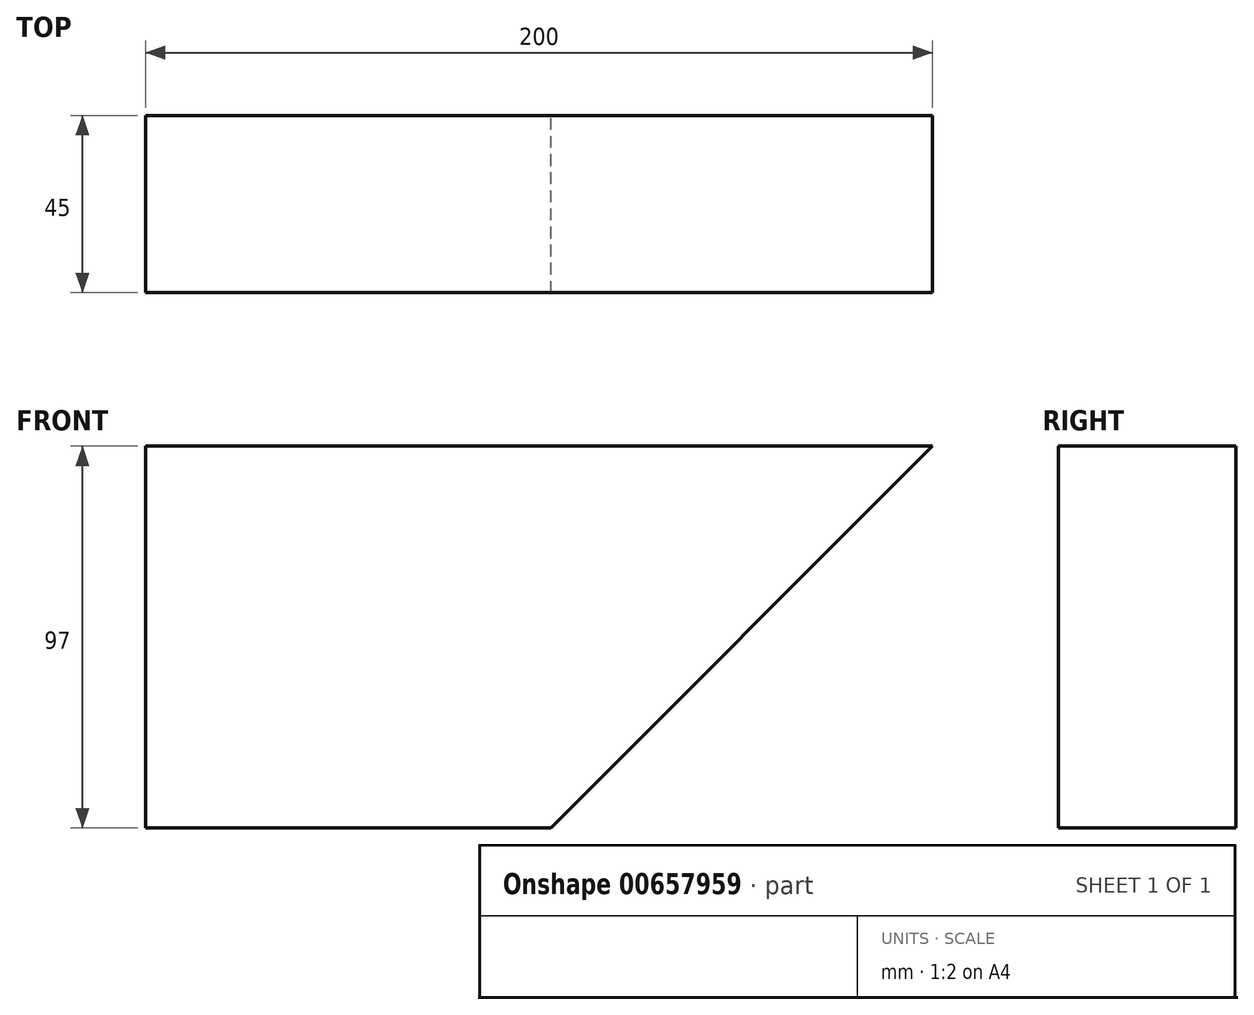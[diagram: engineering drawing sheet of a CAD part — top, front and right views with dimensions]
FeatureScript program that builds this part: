
annotation { "Feature Type Name" : "Feature", "Feature Type Description" : "" }
export const myFeature = defineFeature(function(context is Context, id is Id, definition is map)
    precondition{}
    {
        {
            var Q0;
            Q0=qCreatedBy(makeId("Front.planeOp"),FACE);
            var sketch = newSketch(context, id + "F0", { "sketchPlane" : qUnion([Q0])});
            skLineSegment(sketch, "E0", {"start": v(-100, 48.5) * mm, "end": v(-100, -48.5) * mm});
            skLineSegment(sketch, "E1", {"start": v(-100, -48.5) * mm, "end": v(3, -48.5) * mm});
            skLineSegment(sketch, "E2", {"start": v(3, -48.5) * mm, "end": v(100, 48.5) * mm});
            skLineSegment(sketch, "E3", {"start": v(100, 48.5) * mm, "end": v(-100, 48.5) * mm});
            skLineSegment(sketch, "E4", {"start": v(0, 48.5) * mm, "end": v(0, 0) * mm, "construction": true});
            skLineSegment(sketch, "E5", {"start": v(0, 0) * mm, "end": v(-100, 0) * mm, "construction": true});
            skSolve(sketch);
        }
        {
            var Q0;
            Q0 = qSketchRegion(id + "F0", true);
            extrude(context, id + "F1", {"entities" : qUnion([Q0]), "endBound" : BoundingType.SYMMETRIC, "depth" : 45 * mm, "offsetDistance" : 25 * mm});
        }
    });
